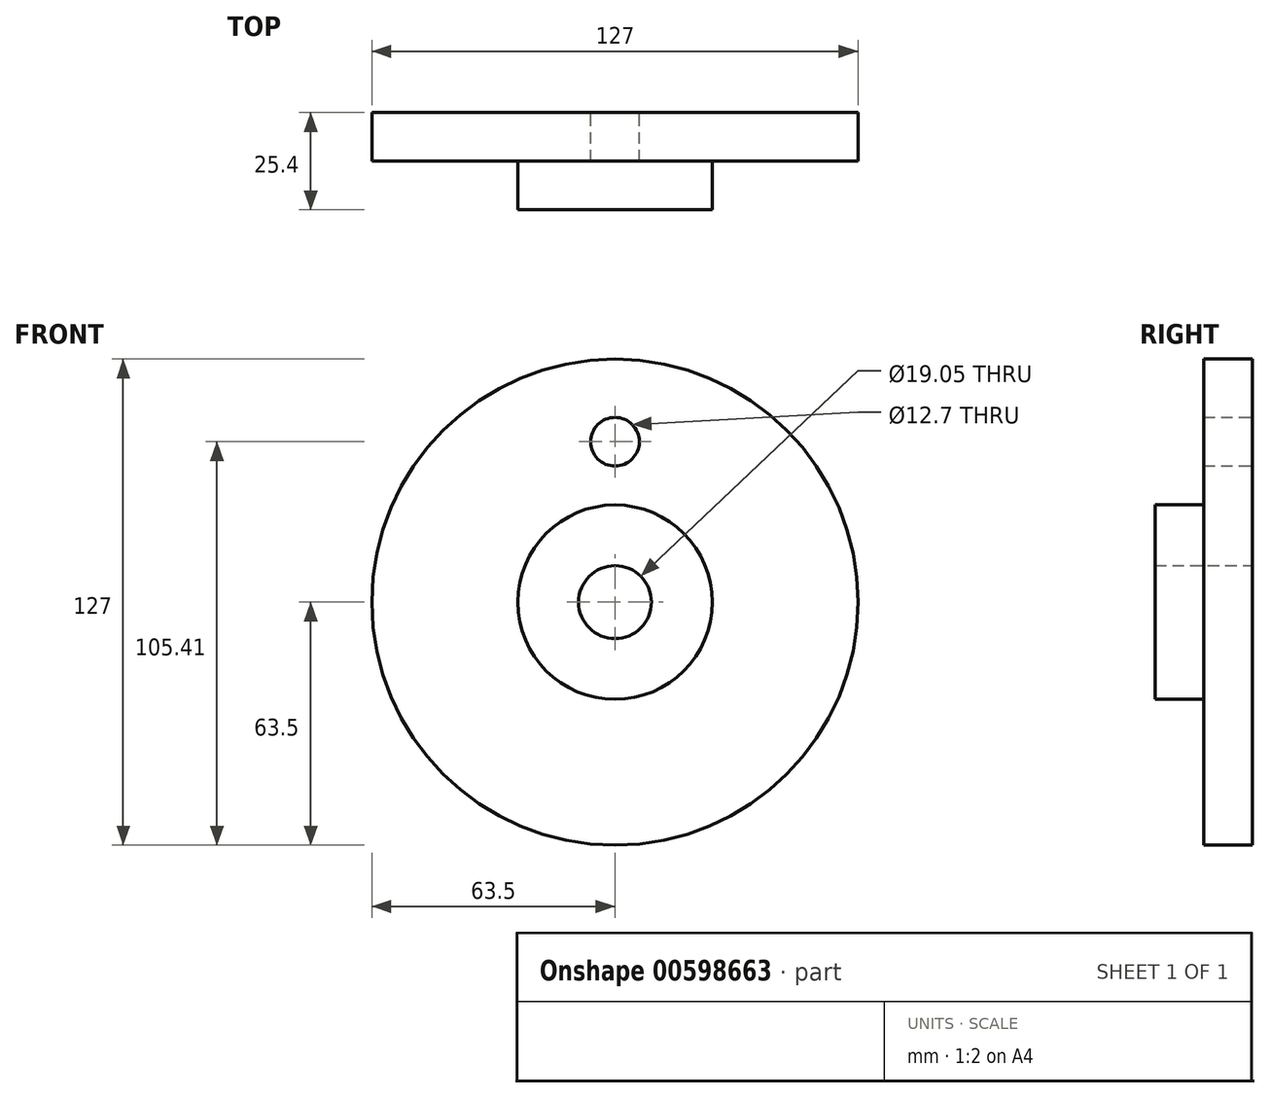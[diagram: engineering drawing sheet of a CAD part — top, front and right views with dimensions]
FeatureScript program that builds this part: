
annotation { "Feature Type Name" : "Feature", "Feature Type Description" : "" }
export const myFeature = defineFeature(function(context is Context, id is Id, definition is map)
    precondition{}
    {
        {
            var Q0;
            Q0=qCreatedBy(makeId("Right.planeOp"),FACE);
            var sketch = newSketch(context, id + "F0", { "sketchPlane" : qUnion([Q0])});
            skLineSegment(sketch, "E0", {"start": v(-25.4, 9.53) * mm, "end": v(0, 9.53) * mm});
            skLineSegment(sketch, "E1", {"start": v(0, 9.53) * mm, "end": v(0, 63.5) * mm});
            skLineSegment(sketch, "E2", {"start": v(0, 63.5) * mm, "end": v(-12.7, 63.5) * mm});
            skLineSegment(sketch, "E3", {"start": v(-12.7, 63.5) * mm, "end": v(-12.7, 25.4) * mm});
            skLineSegment(sketch, "E4", {"start": v(-12.7, 25.4) * mm, "end": v(-25.4, 25.4) * mm});
            skLineSegment(sketch, "E5", {"start": v(-25.4, 25.4) * mm, "end": v(-25.4, 9.53) * mm});
            skLineSegment(sketch, "E6", {"start": v(0, 0) * mm, "end": v(-25.4, 0) * mm, "construction": true});
            skSolve(sketch);
        }
        {
            var Q0;
            Q0 = qSketchRegion(id + "F0", true);
            var Q1;
            Q1=sQuery(id+"F0.wireOp",EDGE,"E6");
            revolve(context, id + "F1", {"entities" : qUnion([Q0]), "axis" : qUnion([Q1]), "revolveType" : RevolveType.FULL});
        }
        {
            var Q0;
            Q0=qCreatedBy(makeId("Front.planeOp"),FACE);
            var sketch = newSketch(context, id + "F2", { "sketchPlane" : qUnion([Q0])});
            skLineSegment(sketch, "E7", {"start": v(0, 0) * mm, "end": v(0, 41.9) * mm, "construction": true});
            skSolve(sketch);
        }
        {
            var Q0;
            Q0=sQuery(id+"F2.wireOp",VERTEX,"E7.end");
            var Q1;
            Q1=makeQuery(id+"F1.opRevolve","SWEPT_BODY",BODY,{"disambiguationData":[OSD([sQuery(id+"F0.wireOp",EDGE,"E0"),sQuery(id+"F0.wireOp",EDGE,"E1"),sQuery(id+"F0.wireOp",EDGE,"E2"),sQuery(id+"F0.wireOp",EDGE,"E3"),sQuery(id+"F0.wireOp",EDGE,"E4"),sQuery(id+"F0.wireOp",EDGE,"E5")])]});
            hole(context, id + "F3", {"style" : HoleStyle.SIMPLE, "endStyle" : HoleEndStyle.THROUGH, "oppositeDirection" : true, "holeDiameter" : 12.7 * mm, "majorDiameter" : 6.35 * mm, "isTappedThrough" : true, "tappedDepth" : 12.7 * mm, "tapClearance" : 3, "locations" : qUnion([Q0]), "scope" : qUnion([Q1])});
        }
    });
